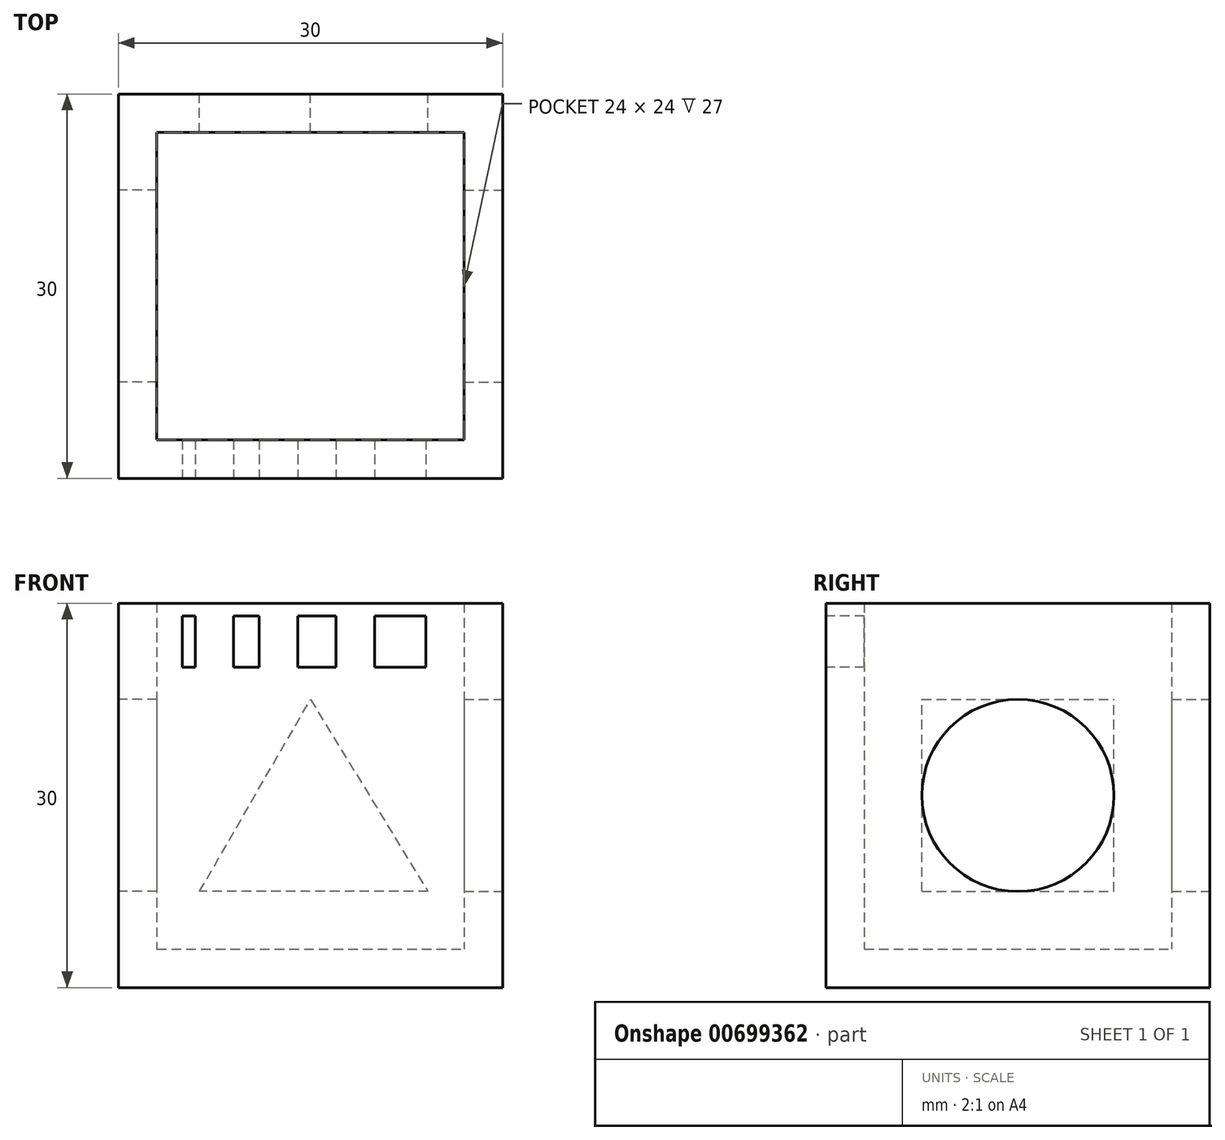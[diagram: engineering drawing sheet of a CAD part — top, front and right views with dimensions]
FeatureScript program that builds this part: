
annotation { "Feature Type Name" : "Feature", "Feature Type Description" : "" }
export const myFeature = defineFeature(function(context is Context, id is Id, definition is map)
    precondition{}
    {
        {
            var Q0;
            Q0=qCreatedBy(makeId("Top.planeOp"),FACE);
            var sketch = newSketch(context, id + "F0", { "sketchPlane" : qUnion([Q0])});
            skLineSegment(sketch, "E0.bottom", {"start": v(-15, -15) * mm, "end": v(15, -15) * mm});
            skLineSegment(sketch, "E0.top", {"start": v(-15, 15) * mm, "end": v(15, 15) * mm});
            skLineSegment(sketch, "E0.left", {"start": v(-15, -15) * mm, "end": v(-15, 15) * mm});
            skLineSegment(sketch, "E0.right", {"start": v(15, -15) * mm, "end": v(15, 15) * mm});
            skPoint(sketch, "E0.middle", {"position": v(0, 0) * mm});
            skSolve(sketch);
        }
        {
            var Q0;
            Q0 = qSketchRegion(id + "F0", true);
            extrude(context, id + "F1", {"entities" : qUnion([Q0]), "depth" : 30 * mm, "offsetDistance" : 25 * mm});
        }
        {
            var Q0;
            Q0=makeQuery(id+"F1.opExtrude","CAP_FACE",FACE,{"disambiguationData":[OSD([sQuery(id+"F0.wireOp",EDGE,"E0.bottom"),sQuery(id+"F0.wireOp",EDGE,"E0.top"),sQuery(id+"F0.wireOp",EDGE,"E0.left"),sQuery(id+"F0.wireOp",EDGE,"E0.right")])],"isStart":false});
            shell(context, id + "F2", {"entities" : qUnion([Q0]), "thickness" : 3 * mm});
        }
        {
            var Q0;
            Q0=makeQuery(id+"F1.opExtrude","SWEPT_FACE",FACE,{"disambiguationData":[OSD([sQuery(id+"F0.wireOp",EDGE,"E0.left")])]});
            var sketch = newSketch(context, id + "F3", { "sketchPlane" : qUnion([Q0])});
            skLineSegment(sketch, "E1.bottom", {"start": v(7.5, 7.5) * mm, "end": v(-7.5, 7.5) * mm});
            skLineSegment(sketch, "E1.top", {"start": v(7.5, 22.5) * mm, "end": v(-7.5, 22.5) * mm});
            skLineSegment(sketch, "E1.left", {"start": v(7.5, 7.5) * mm, "end": v(7.5, 22.5) * mm});
            skLineSegment(sketch, "E1.right", {"start": v(-7.5, 7.5) * mm, "end": v(-7.5, 22.5) * mm});
            skPoint(sketch, "E1.middle", {"position": v(0, 15) * mm});
            skSolve(sketch);
        }
        {
            var Q0;
            Q0=makeQuery(id+"F3.imprint","IMPRINT",FACE,{"disambiguationData":[TD([[makeQuery(id+"F3.imprint","IMPRINT",EDGE,{"derivedFrom":sQuery(id+"F3.wireOp",EDGE,"E1.bottom")}),-1.0]])]});
            extrude(context, id + "F4", {"entities" : qUnion([Q0]), "operationType" : NewBodyOperationType.REMOVE, "endBound" : BoundingType.UP_TO_NEXT, "oppositeDirection" : true, "depth" : 25 * mm, "offsetDistance" : 25 * mm});
        }
        {
            var Q0;
            Q0=makeQuery(id+"F1.opExtrude","SWEPT_FACE",FACE,{"disambiguationData":[OSD([sQuery(id+"F0.wireOp",EDGE,"E0.right")])]});
            var sketch = newSketch(context, id + "F5", { "sketchPlane" : qUnion([Q0])});
            skCircle(sketch, "E2", {"center": v(0, 15) * mm, "radius": 7.5 * mm});
            skSolve(sketch);
        }
        {
            var Q0;
            Q0=makeQuery(id+"F5.imprint","IMPRINT",FACE,{"disambiguationData":[TD([[makeQuery(id+"F5.imprint","IMPRINT",EDGE,{"derivedFrom":sQuery(id+"F5.wireOp",EDGE,"E2")}),1.0]])]});
            extrude(context, id + "F6", {"entities" : qUnion([Q0]), "operationType" : NewBodyOperationType.REMOVE, "endBound" : BoundingType.UP_TO_NEXT, "oppositeDirection" : true, "depth" : 25 * mm, "offsetDistance" : 25 * mm});
        }
        {
            var Q0;
            Q0=makeQuery(id+"F1.opExtrude","SWEPT_FACE",FACE,{"disambiguationData":[OSD([sQuery(id+"F0.wireOp",EDGE,"E0.top")])]});
            var sketch = newSketch(context, id + "F7", { "sketchPlane" : qUnion([Q0])});
            skLineSegment(sketch, "E3", {"start": v(0, 22.5) * mm, "end": v(-9.18, 7.5) * mm});
            skLineSegment(sketch, "E4", {"start": v(-9.18, 7.5) * mm, "end": v(8.66, 7.5) * mm});
            skLineSegment(sketch, "E5", {"start": v(8.66, 7.5) * mm, "end": v(0, 22.5) * mm});
            skSolve(sketch);
        }
        {
            var Q0;
            Q0=makeQuery(id+"F7.imprint","IMPRINT",FACE,{"disambiguationData":[TD([[makeQuery(id+"F7.imprint","IMPRINT",EDGE,{"derivedFrom":sQuery(id+"F7.wireOp",EDGE,"E3")}),1.0]])]});
            extrude(context, id + "F8", {"entities" : qUnion([Q0]), "operationType" : NewBodyOperationType.REMOVE, "endBound" : BoundingType.UP_TO_NEXT, "oppositeDirection" : true, "depth" : 25 * mm, "offsetDistance" : 25 * mm});
        }
        {
            var Q0;
            Q0=makeQuery(id+"F1.opExtrude","SWEPT_FACE",FACE,{"disambiguationData":[OSD([sQuery(id+"F0.wireOp",EDGE,"E0.bottom")])]});
            var sketch = newSketch(context, id + "F9", { "sketchPlane" : qUnion([Q0])});
            skLineSegment(sketch, "E6.bottom", {"start": v(-9, 29) * mm, "end": v(-10, 29) * mm});
            skLineSegment(sketch, "E6.top", {"start": v(-9, 25) * mm, "end": v(-10, 25) * mm});
            skLineSegment(sketch, "E6.left", {"start": v(-9, 29) * mm, "end": v(-9, 25) * mm});
            skLineSegment(sketch, "E6.right", {"start": v(-10, 29) * mm, "end": v(-10, 25) * mm});
            skPoint(sketch, "E6.middle", {"position": v(-9.5, 27) * mm});
            skLineSegment(sketch, "E7.bottom", {"start": v(-4, 29) * mm, "end": v(-6, 29) * mm});
            skLineSegment(sketch, "E7.top", {"start": v(-4, 25) * mm, "end": v(-6, 25) * mm});
            skLineSegment(sketch, "E7.left", {"start": v(-4, 29) * mm, "end": v(-4, 25) * mm});
            skLineSegment(sketch, "E7.right", {"start": v(-6, 29) * mm, "end": v(-6, 25) * mm});
            skPoint(sketch, "E7.middle", {"position": v(-5, 27) * mm});
            skLineSegment(sketch, "E8.bottom", {"start": v(2, 29) * mm, "end": v(-1, 29) * mm});
            skLineSegment(sketch, "E8.top", {"start": v(2, 25) * mm, "end": v(-1, 25) * mm});
            skLineSegment(sketch, "E8.left", {"start": v(2, 29) * mm, "end": v(2, 25) * mm});
            skLineSegment(sketch, "E8.right", {"start": v(-1, 29) * mm, "end": v(-1, 25) * mm});
            skPoint(sketch, "E8.middle", {"position": v(0.5, 27) * mm});
            skLineSegment(sketch, "E9.bottom", {"start": v(9, 29) * mm, "end": v(5, 29) * mm});
            skLineSegment(sketch, "E9.top", {"start": v(9, 25) * mm, "end": v(5, 25) * mm});
            skLineSegment(sketch, "E9.left", {"start": v(9, 29) * mm, "end": v(9, 25) * mm});
            skLineSegment(sketch, "E9.right", {"start": v(5, 29) * mm, "end": v(5, 25) * mm});
            skPoint(sketch, "E9.middle", {"position": v(7, 27) * mm});
            skSolve(sketch);
        }
        {
            var Q0;
            Q0=makeQuery(id+"F9.imprint","IMPRINT",FACE,{"disambiguationData":[TD([[makeQuery(id+"F9.imprint","IMPRINT",EDGE,{"derivedFrom":sQuery(id+"F9.wireOp",EDGE,"E6.bottom")}),1.0]])]});
            var Q1;
            Q1=makeQuery(id+"F9.imprint","IMPRINT",FACE,{"disambiguationData":[TD([[makeQuery(id+"F9.imprint","IMPRINT",EDGE,{"derivedFrom":sQuery(id+"F9.wireOp",EDGE,"E7.bottom")}),1.0]])]});
            var Q2;
            Q2=makeQuery(id+"F9.imprint","IMPRINT",FACE,{"disambiguationData":[TD([[makeQuery(id+"F9.imprint","IMPRINT",EDGE,{"derivedFrom":sQuery(id+"F9.wireOp",EDGE,"E8.bottom")}),1.0]])]});
            var Q3;
            Q3=makeQuery(id+"F9.imprint","IMPRINT",FACE,{"disambiguationData":[TD([[makeQuery(id+"F9.imprint","IMPRINT",EDGE,{"derivedFrom":sQuery(id+"F9.wireOp",EDGE,"E9.bottom")}),1.0]])]});
            extrude(context, id + "F10", {"entities" : qUnion([Q0, Q1, Q2, Q3]), "operationType" : NewBodyOperationType.REMOVE, "oppositeDirection" : true, "depth" : 4 * mm, "offsetDistance" : 25 * mm});
        }
    });
